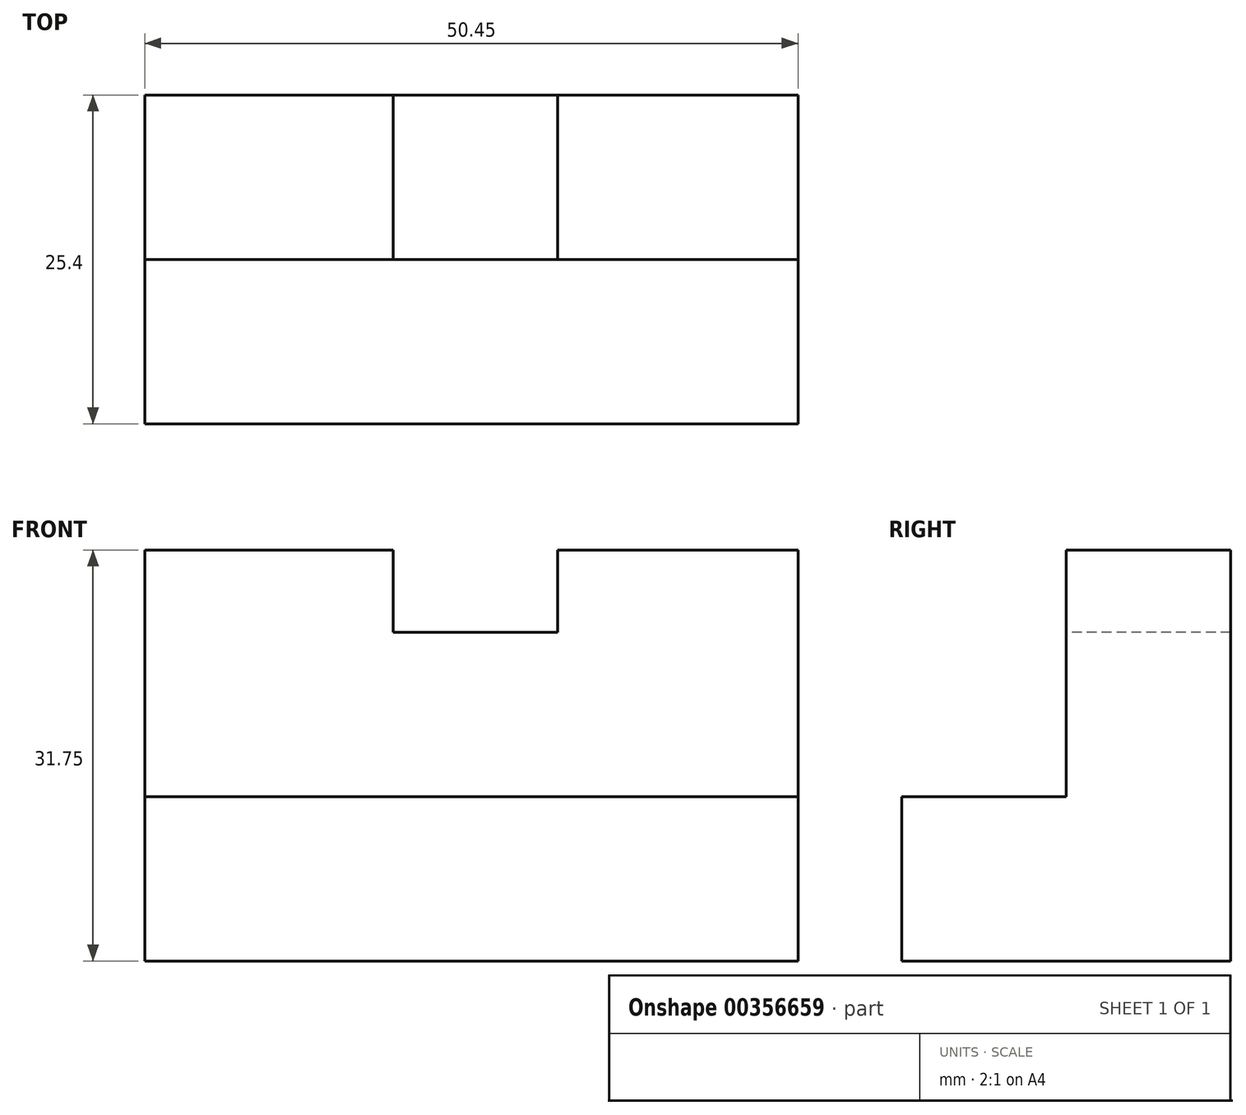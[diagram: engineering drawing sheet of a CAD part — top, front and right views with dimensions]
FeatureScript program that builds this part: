
annotation { "Feature Type Name" : "Feature", "Feature Type Description" : "" }
export const myFeature = defineFeature(function(context is Context, id is Id, definition is map)
    precondition{}
    {
        {
            var Q0;
            Q0=qCreatedBy(makeId("Right.planeOp"),FACE);
            var sketch = newSketch(context, id + "F0", { "sketchPlane" : qUnion([Q0])});
            skLineSegment(sketch, "E0", {"start": v(-12.7, -12.7) * mm, "end": v(12.7, -12.7) * mm});
            skLineSegment(sketch, "E1", {"start": v(12.7, -12.7) * mm, "end": v(12.7, 19.05) * mm});
            skLineSegment(sketch, "E2", {"start": v(12.7, 19.05) * mm, "end": v(0, 19.05) * mm});
            skLineSegment(sketch, "E3", {"start": v(0, 19.05) * mm, "end": v(0, 0) * mm});
            skLineSegment(sketch, "E4", {"start": v(0, 0) * mm, "end": v(-12.7, 0) * mm});
            skLineSegment(sketch, "E5", {"start": v(-12.7, 0) * mm, "end": v(-12.7, -12.7) * mm});
            skSolve(sketch);
        }
        {
            var Q0;
            Q0=makeQuery(id+"F0.imprint","IMPRINT",FACE,{"disambiguationData":[TD([[makeQuery(id+"F0.imprint","IMPRINT",EDGE,{"derivedFrom":sQuery(id+"F0.wireOp",EDGE,"E0")}),1.0]])]});
            extrude(context, id + "F1", {"entities" : qUnion([Q0]), "depth" : 25.4 * mm});
        }
        {
            var Q0;
            Q0=makeQuery(id+"F1.opExtrude","CAP_FACE",FACE,{"disambiguationData":[OSD([sQuery(id+"F0.wireOp",EDGE,"E0"),sQuery(id+"F0.wireOp",EDGE,"E1"),sQuery(id+"F0.wireOp",EDGE,"E2"),sQuery(id+"F0.wireOp",EDGE,"E3"),sQuery(id+"F0.wireOp",EDGE,"E4"),sQuery(id+"F0.wireOp",EDGE,"E5")])],"isStart":false});
            extrude(context, id + "F2", {"entities" : qUnion([Q0]), "operationType" : NewBodyOperationType.ADD, "depth" : 38.1 * mm});
        }
        {
            var Q0;
            {var subQ0=sQuery(id+"F0.wireOp",EDGE,"E3");Q0=makeQuery(id+"F2.boolean.opBoolean","MERGE",FACE,{"derivedFrom":[makeQuery(id+"F1.opExtrude","SWEPT_FACE",FACE,{"disambiguationData":[OSD([subQ0])]}),makeQuery(id+"F2.opExtrude","SWEPT_FACE",FACE,{"disambiguationData":[OSD([subQ0])]})]});}
            var sketch = newSketch(context, id + "F3", { "sketchPlane" : qUnion([Q0])});
            skLineSegment(sketch, "E6", {"start": v(19.2, 19.05) * mm, "end": v(19.2, 12.7) * mm});
            skLineSegment(sketch, "E7", {"start": v(19.2, 12.7) * mm, "end": v(31.9, 12.7) * mm});
            skLineSegment(sketch, "E8", {"start": v(31.9, 12.7) * mm, "end": v(31.9, 19.05) * mm});
            skSolve(sketch);
        }
        {
            var Q0;
            {var subQ0=sQuery(id+"F3.wireOp",EDGE,"E6");Q0=makeQuery(id+"F3.imprint","IMPRINT",FACE,{"disambiguationData":[TD([[makeQuery(id+"F3.imprint","IMPRINT",EDGE,{"derivedFrom":subQ0}),1.0]])]});}
            extrude(context, id + "F4", {"entities" : qUnion([Q0]), "operationType" : NewBodyOperationType.REMOVE, "oppositeDirection" : true, "depth" : 12.7 * mm});
        }
        {
            var Q0;
            {var subQ0=sQuery(id+"F0.wireOp",EDGE,"E3");Q0=makeQuery(id+"F2.boolean.opBoolean","MERGE",FACE,{"derivedFrom":[makeQuery(id+"F1.opExtrude","SWEPT_FACE",FACE,{"disambiguationData":[OSD([subQ0])]}),makeQuery(id+"F2.opExtrude","SWEPT_FACE",FACE,{"disambiguationData":[OSD([subQ0])]})]});}
            var sketch = newSketch(context, id + "F5", { "sketchPlane" : qUnion([Q0])});
            skLineSegment(sketch, "E9", {"start": v(50.45, 19.05) * mm, "end": v(50.45, 0) * mm});
            skLineSegment(sketch, "E10", {"start": v(50.45, 0) * mm, "end": v(50.45, -13.46) * mm});
            skSolve(sketch);
        }
        {
            var Q0;
            {var subQ0=sQuery(id+"F5.wireOp",EDGE,"E9");Q0=makeQuery(id+"F5.imprint","IMPRINT",FACE,{"disambiguationData":[TD([[makeQuery(id+"F5.imprint","IMPRINT",EDGE,{"derivedFrom":subQ0}),1.0]])]});}
            extrude(context, id + "F6", {"entities" : qUnion([Q0]), "operationType" : NewBodyOperationType.REMOVE, "oppositeDirection" : true, "depth" : 25.4 * mm});
        }
        {
            var Q0;
            {var subQ0=sQuery(id+"F0.wireOp",EDGE,"E5");Q0=makeQuery(id+"F2.boolean.opBoolean","MERGE",FACE,{"derivedFrom":[makeQuery(id+"F1.opExtrude","SWEPT_FACE",FACE,{"disambiguationData":[OSD([subQ0])]}),makeQuery(id+"F2.opExtrude","SWEPT_FACE",FACE,{"disambiguationData":[OSD([subQ0])]})]});}
            var sketch = newSketch(context, id + "F7", { "sketchPlane" : qUnion([Q0])});
            skLineSegment(sketch, "E11", {"start": v(50.45, 0) * mm, "end": v(50.45, -12.7) * mm});
            skSolve(sketch);
        }
        {
            var Q0;
            {var subQ0=sQuery(id+"F7.wireOp",EDGE,"E11");Q0=makeQuery(id+"F7.imprint","IMPRINT",FACE,{"disambiguationData":[TD([[makeQuery(id+"F7.imprint","IMPRINT",EDGE,{"derivedFrom":subQ0}),1.0]])]});}
            extrude(context, id + "F8", {"entities" : qUnion([Q0]), "operationType" : NewBodyOperationType.REMOVE, "oppositeDirection" : true, "depth" : 25.4 * mm});
        }
    });
